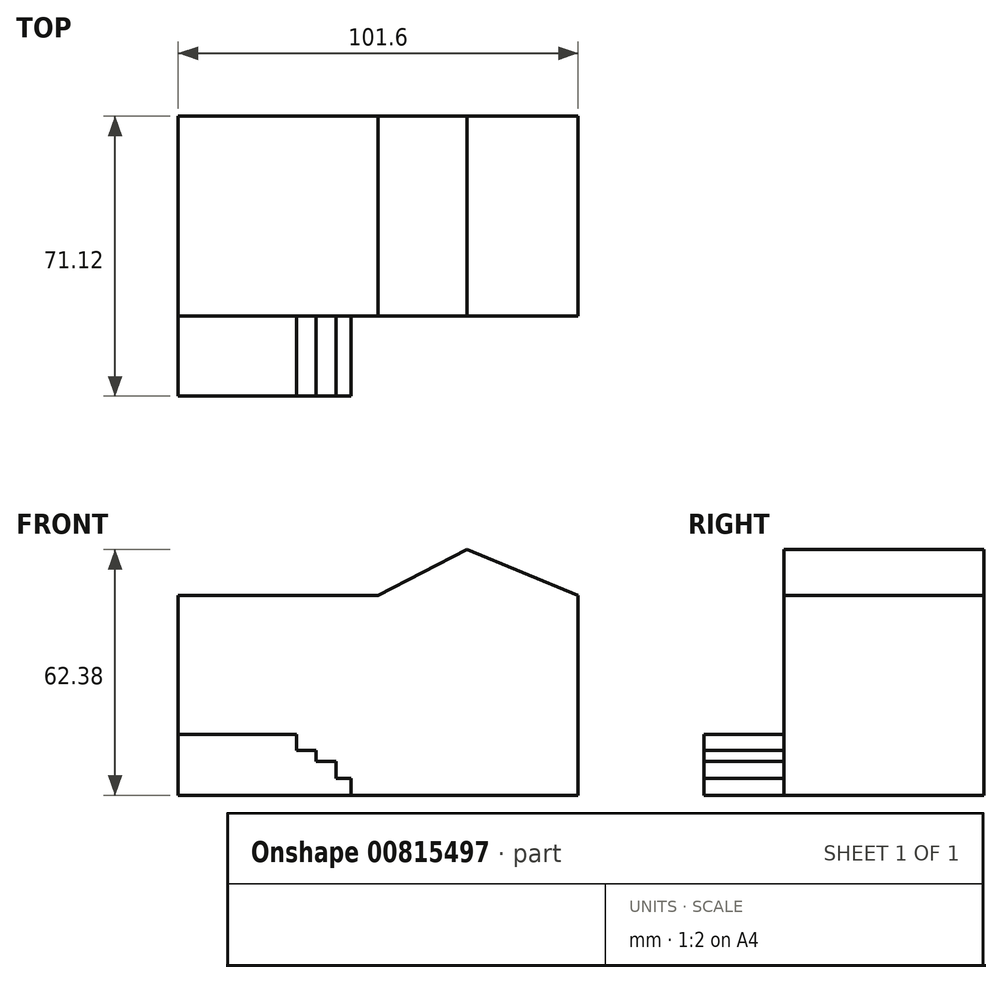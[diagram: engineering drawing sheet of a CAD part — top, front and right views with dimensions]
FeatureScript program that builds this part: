
annotation { "Feature Type Name" : "Feature", "Feature Type Description" : "" }
export const myFeature = defineFeature(function(context is Context, id is Id, definition is map)
    precondition{}
    {
        {
            var Q0;
            Q0=qCreatedBy(makeId("Front.planeOp"),FACE);
            var sketch = newSketch(context, id + "F0", { "sketchPlane" : qUnion([Q0])});
            skLineSegment(sketch, "E0.bottom", {"start": v(-50.8, 25.4) * mm, "end": v(50.8, 25.4) * mm});
            skLineSegment(sketch, "E0.top", {"start": v(-50.8, -25.4) * mm, "end": v(50.8, -25.4) * mm});
            skLineSegment(sketch, "E0.left", {"start": v(-50.8, 25.4) * mm, "end": v(-50.8, -25.4) * mm});
            skLineSegment(sketch, "E0.right", {"start": v(50.8, 25.4) * mm, "end": v(50.8, -25.4) * mm});
            skLineSegment(sketch, "E1", {"start": v(0, 25.4) * mm, "end": v(22.6, 36.98) * mm});
            skLineSegment(sketch, "E2", {"start": v(22.6, 36.98) * mm, "end": v(50.8, 25.4) * mm});
            skSolve(sketch);
        }
        {
            var Q0;
            Q0 = qSketchRegion(id + "F0", true);
            extrude(context, id + "F1", {"entities" : qUnion([Q0]), "endBound" : BoundingType.SYMMETRIC, "depth" : 50.8 * mm, "offsetDistance" : 25.4 * mm});
        }
        {
            var Q0;
            Q0=qCreatedBy(makeId("Front.planeOp"),FACE);
            var sketch = newSketch(context, id + "F2", { "sketchPlane" : qUnion([Q0])});
            skLineSegment(sketch, "E3.bottom", {"start": v(-50.8, -9.97) * mm, "end": v(-20.69, -9.97) * mm});
            skLineSegment(sketch, "E3.top", {"start": v(-50.8, -25.4) * mm, "end": v(-20.69, -25.4) * mm});
            skLineSegment(sketch, "E3.left", {"start": v(-50.8, -9.97) * mm, "end": v(-50.8, -25.4) * mm});
            skLineSegment(sketch, "E3.right", {"start": v(-20.69, -9.97) * mm, "end": v(-20.69, -25.4) * mm});
            skLineSegment(sketch, "E4.bottom", {"start": v(-20.69, -13.98) * mm, "end": v(-15.81, -13.98) * mm});
            skLineSegment(sketch, "E4.top", {"start": v(-20.69, -25.4) * mm, "end": v(-15.81, -25.4) * mm});
            skLineSegment(sketch, "E4.left", {"start": v(-20.69, -13.98) * mm, "end": v(-20.69, -25.4) * mm});
            skLineSegment(sketch, "E4.right", {"start": v(-15.81, -13.98) * mm, "end": v(-15.81, -25.4) * mm});
            skLineSegment(sketch, "E5.bottom", {"start": v(-15.81, -16.8) * mm, "end": v(-10.65, -16.8) * mm});
            skLineSegment(sketch, "E5.top", {"start": v(-15.81, -25.4) * mm, "end": v(-10.65, -25.4) * mm});
            skLineSegment(sketch, "E5.left", {"start": v(-15.81, -16.8) * mm, "end": v(-15.81, -25.4) * mm});
            skLineSegment(sketch, "E5.right", {"start": v(-10.65, -16.8) * mm, "end": v(-10.65, -25.4) * mm});
            skLineSegment(sketch, "E6.bottom", {"start": v(-10.65, -21.1) * mm, "end": v(-6.92, -21.1) * mm});
            skLineSegment(sketch, "E6.top", {"start": v(-10.65, -25.4) * mm, "end": v(-6.92, -25.4) * mm});
            skLineSegment(sketch, "E6.left", {"start": v(-10.65, -21.1) * mm, "end": v(-10.65, -25.4) * mm});
            skLineSegment(sketch, "E6.right", {"start": v(-6.92, -21.1) * mm, "end": v(-6.92, -25.4) * mm});
            skSolve(sketch);
        }
        {
            var Q0;
            Q0 = qSketchRegion(id + "F2", true);
            extrude(context, id + "F3", {"entities" : qUnion([Q0]), "operationType" : NewBodyOperationType.ADD, "depth" : 45.72 * mm, "offsetDistance" : 25.4 * mm});
        }
    });
